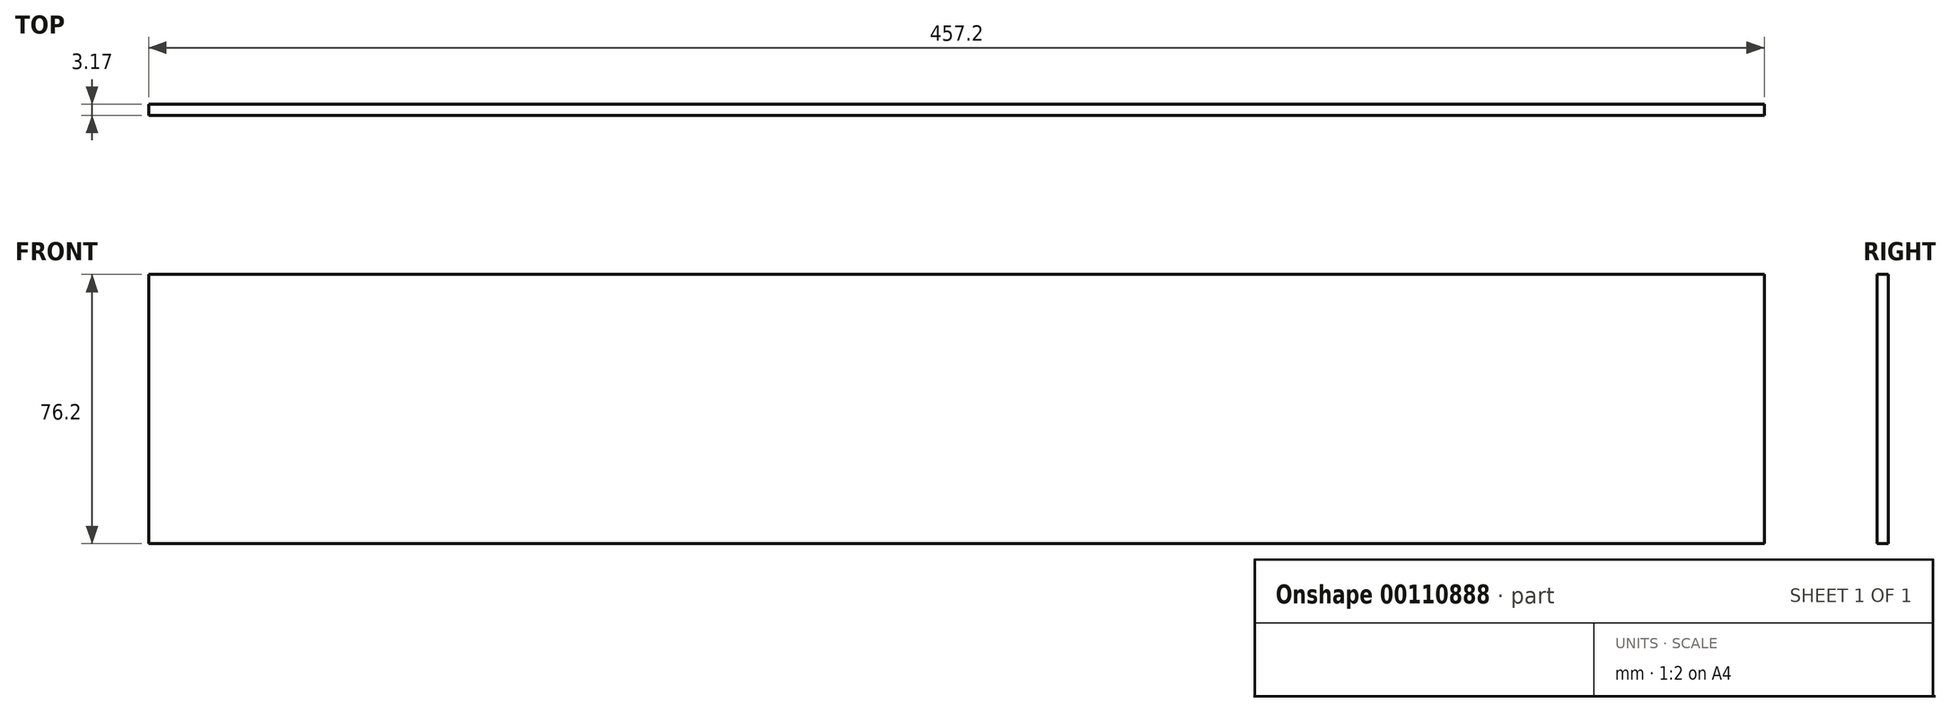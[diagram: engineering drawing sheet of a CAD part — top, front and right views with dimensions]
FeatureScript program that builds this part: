
annotation { "Feature Type Name" : "Feature", "Feature Type Description" : "" }
export const myFeature = defineFeature(function(context is Context, id is Id, definition is map)
    precondition{}
    {
        {
            var Q0;
            Q0=qCreatedBy(makeId("Front.planeOp"),FACE);
            var sketch = newSketch(context, id + "F0", { "sketchPlane" : qUnion([Q0])});
            skLineSegment(sketch, "E0.bottom", {"start": v(0, 0) * mm, "end": v(-457.2, 0) * mm});
            skLineSegment(sketch, "E0.top", {"start": v(0, 76.2) * mm, "end": v(-457.2, 76.2) * mm});
            skLineSegment(sketch, "E0.left", {"start": v(0, 0) * mm, "end": v(0, 76.2) * mm});
            skLineSegment(sketch, "E0.right", {"start": v(-457.2, 0) * mm, "end": v(-457.2, 76.2) * mm});
            skSolve(sketch);
        }
        {
            var Q0;
            Q0 = qSketchRegion(id + "F0", true);
            extrude(context, id + "F1", {"entities" : qUnion([Q0]), "depth" : 3.17 * mm});
        }
    });
